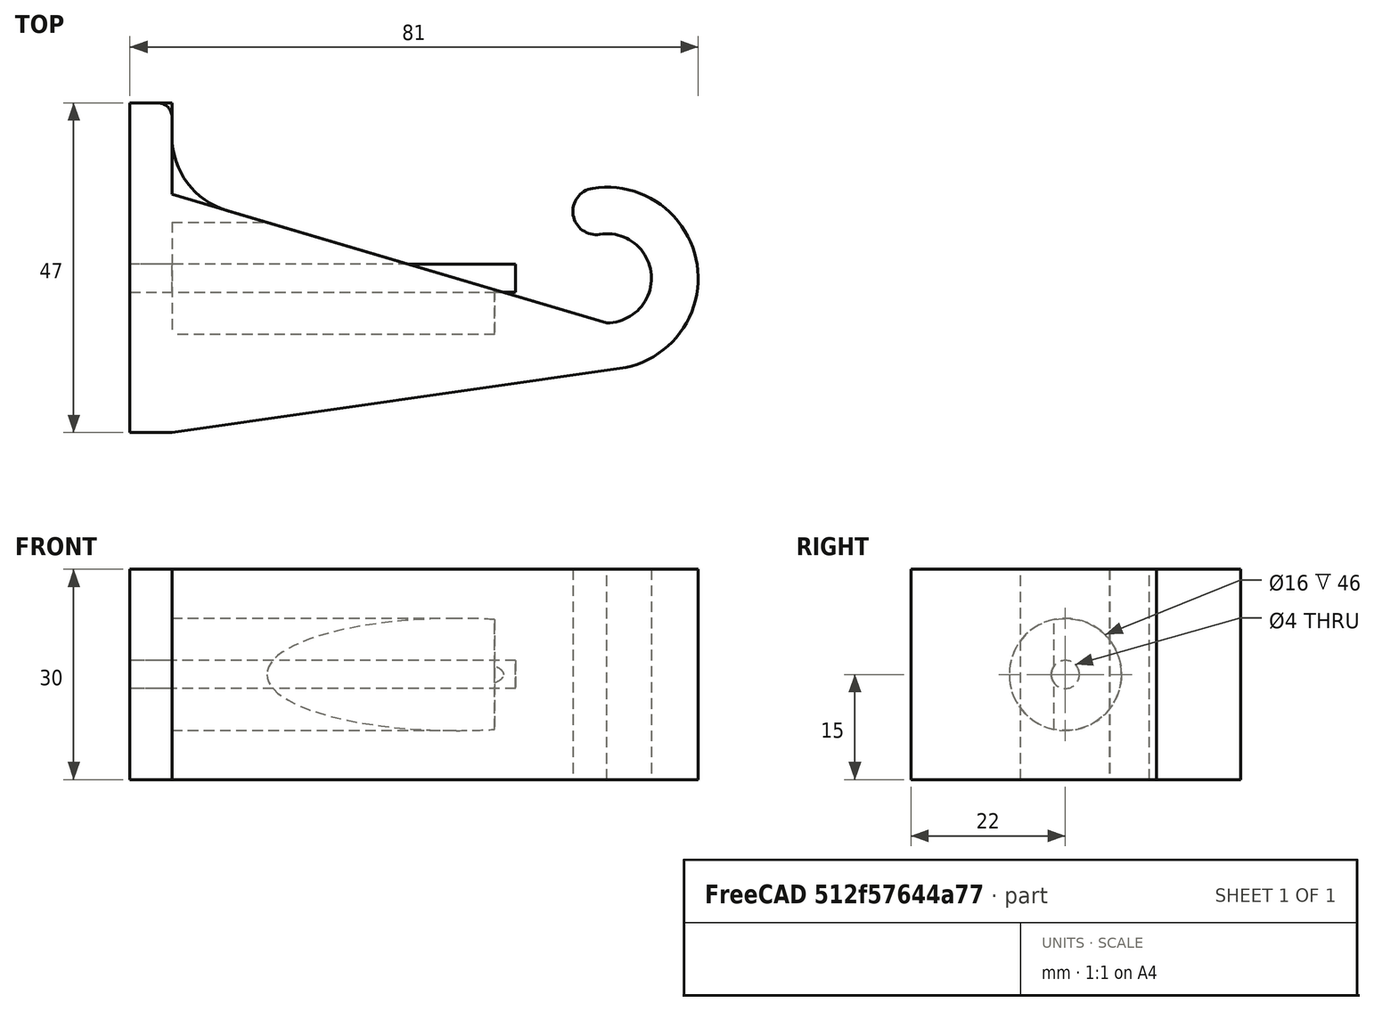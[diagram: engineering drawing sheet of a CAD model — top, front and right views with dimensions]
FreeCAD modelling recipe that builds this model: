
FCSTD DOCUMENT  (FreeCAD 0.16R)
Label: BabyGateLong
License: All rights reserved
LicenseURL: http://en.wikipedia.org/wiki/All_rights_reserved
objects: Sketcher::SketchObject×3, PartDesign::Pocket×2, PartDesign::Fillet×2, PartDesign::Pad×1, Mesh::Feature×1
note: 11 computed .brp shape members not serialized (recipe doc carries the construction recipe); baked Part::Feature solids carry a one-line shape summary decoded from their .brp

FEATURE [Sketcher::SketchObject] Sketch001
  sketch-geometry (9):
    g0: ArcOfCircle CenterX=0 CenterY=0 CenterZ=0 NormalX=0 NormalY=0 NormalZ=1 Radius=6.35 StartAngle=4.71239 EndAngle=8.01212
    g1: ArcOfCircle CenterX=0 CenterY=0 CenterZ=0 NormalX=0 NormalY=0 NormalZ=1 Radius=13 StartAngle=4.85445 EndAngle=8.01212
    g2: LineSegment StartX=1.84063 StartY=-12.869 StartZ=0 EndX=-62 EndY=-22 EndZ=0
    g3: LineSegment StartX=2e-12 StartY=-6.35 StartZ=0 EndX=-62 EndY=12 EndZ=0
    g4: LineSegment StartX=-62 StartY=12 StartZ=0 EndX=-62 EndY=25 EndZ=0
    g5: LineSegment StartX=-62 StartY=25 StartZ=0 EndX=-68 EndY=25 EndZ=0
    g6: LineSegment StartX=-68 StartY=25 StartZ=0 EndX=-68 EndY=-22 EndZ=0
    g7: LineSegment StartX=-68 StartY=-22 StartZ=0 EndX=-62 EndY=-22 EndZ=0
    g8: ArcOfCircle CenterX=-1.52364 CenterY=9.55427 CenterZ=0 NormalX=0 NormalY=0 NormalZ=1 Radius=3.325 StartAngle=1.72894 EndAngle=4.87053
  constraints (28):
    c: Coincident(g0,g-1)
    c: PointOnObject(g0,g-2)
    c: Radius(g0) = 6.35
    c: DistanceX(g0,g-1) = 1
    c: Radius(g1) = 13
    c: Coincident(g1,g-1)
    c: Coincident(g2,g1)
    c: DistanceX(g3) = -62
    c: DistanceX(g2) = -62
    c: Coincident(g4,g3)
    c: Vertical(g4)
    c: Coincident(g4,g5)
    c: Coincident(g5,g6)
    c: Vertical(g6)
    c: Coincident(g6,g7)
    c: Horizontal(g5)
    c: Horizontal(g7)
    c: DistanceX(g5,g5) = 6
    c: Tangent(g8,g1)
    c: Coincident(g8,g1)
    c: Coincident(g0,g8)
    c: Coincident(g2,g7)
    c: Tangent(g2,g1)
    c: DistanceY(g5) = 25
    c: DistanceY(g6) = -22
    c: Coincident(g3,g0)
    c: Tangent(g0,g8)
    c: DistanceY(g3) = 12
FEATURE [PartDesign::Pad] Pad
  Length = 30
  Length2 = 100
  Sketch = -> Sketch001
  Type = 0
FEATURE [Sketcher::SketchObject] Sketch002
  Placement = pos=(-68,0,0) rot=(0.57735,-0.57735,-0.57735;2.0944rad)
  Support = -> Pad [Face7]
  sketch-geometry (1):
    g0: Circle CenterX=0 CenterY=15 CenterZ=0 NormalX=0 NormalY=0 NormalZ=1 Radius=2
  constraints (3):
    c: PointOnObject(g0,g-2)
    c: DistanceY(g-1,g0) = 15
    c: Radius(g0) = 2
FEATURE [PartDesign::Pocket] Pocket
  Length = 55
  Sketch = -> Sketch002
  Type = 0
FEATURE [Sketcher::SketchObject] Sketch003
  Placement = pos=(-62,0,0) rot=(0.57735,0.57735,0.57735;2.0944rad)
  Support = -> Pocket [Face5]
  sketch-geometry (1):
    g0: Circle CenterX=0 CenterY=15 CenterZ=0 NormalX=0 NormalY=0 NormalZ=1 Radius=8
  constraints (3):
    c: PointOnObject(g0,g-2)
    c: DistanceY(g0) = 15
    c: Radius(g0) = 8
FEATURE [PartDesign::Pocket] Pocket001
  Length = 46
  Reversed = true
  Sketch = -> Sketch003
  Type = 0
FEATURE [PartDesign::Fillet] Fillet
  Base = -> Pocket001 [Edge4]
  Radius = 11
FEATURE [PartDesign::Fillet] Fillet001
  Base = -> Fillet [Edge37]
  Radius = 2
FEATURE [Mesh::Feature] Mesh  label="Fillet001 (Meshed)"
